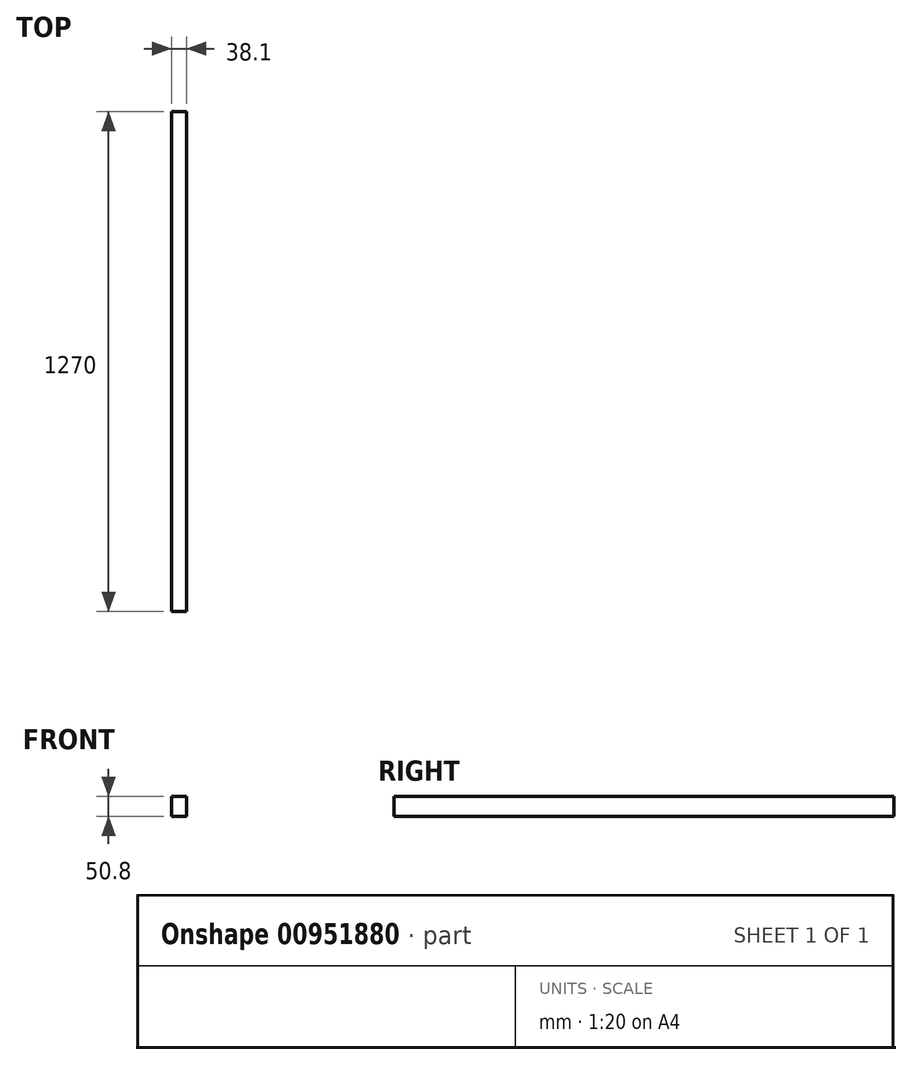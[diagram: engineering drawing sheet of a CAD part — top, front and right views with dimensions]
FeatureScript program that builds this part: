
annotation { "Feature Type Name" : "Feature", "Feature Type Description" : "" }
export const myFeature = defineFeature(function(context is Context, id is Id, definition is map)
    precondition{}
    {
        {
            var Q0;
            Q0=qCreatedBy(makeId("Top.planeOp"),FACE);
            var sketch = newSketch(context, id + "F0", { "sketchPlane" : qUnion([Q0])});
            skLineSegment(sketch, "E0.bottom", {"start": v(-19.05, 635) * mm, "end": v(19.05, 635) * mm});
            skLineSegment(sketch, "E0.top", {"start": v(-19.05, -635) * mm, "end": v(19.05, -635) * mm});
            skLineSegment(sketch, "E0.left", {"start": v(-19.05, 635) * mm, "end": v(-19.05, -635) * mm});
            skLineSegment(sketch, "E0.right", {"start": v(19.05, 635) * mm, "end": v(19.05, -635) * mm});
            skPoint(sketch, "E0.middle", {"position": v(0, 0) * mm});
            skSolve(sketch);
        }
        {
            var Q0;
            Q0 = qSketchRegion(id + "F0", true);
            extrude(context, id + "F1", {"entities" : qUnion([Q0]), "depth" : 50.8 * mm, "offsetDistance" : 25.4 * mm});
        }
    });
